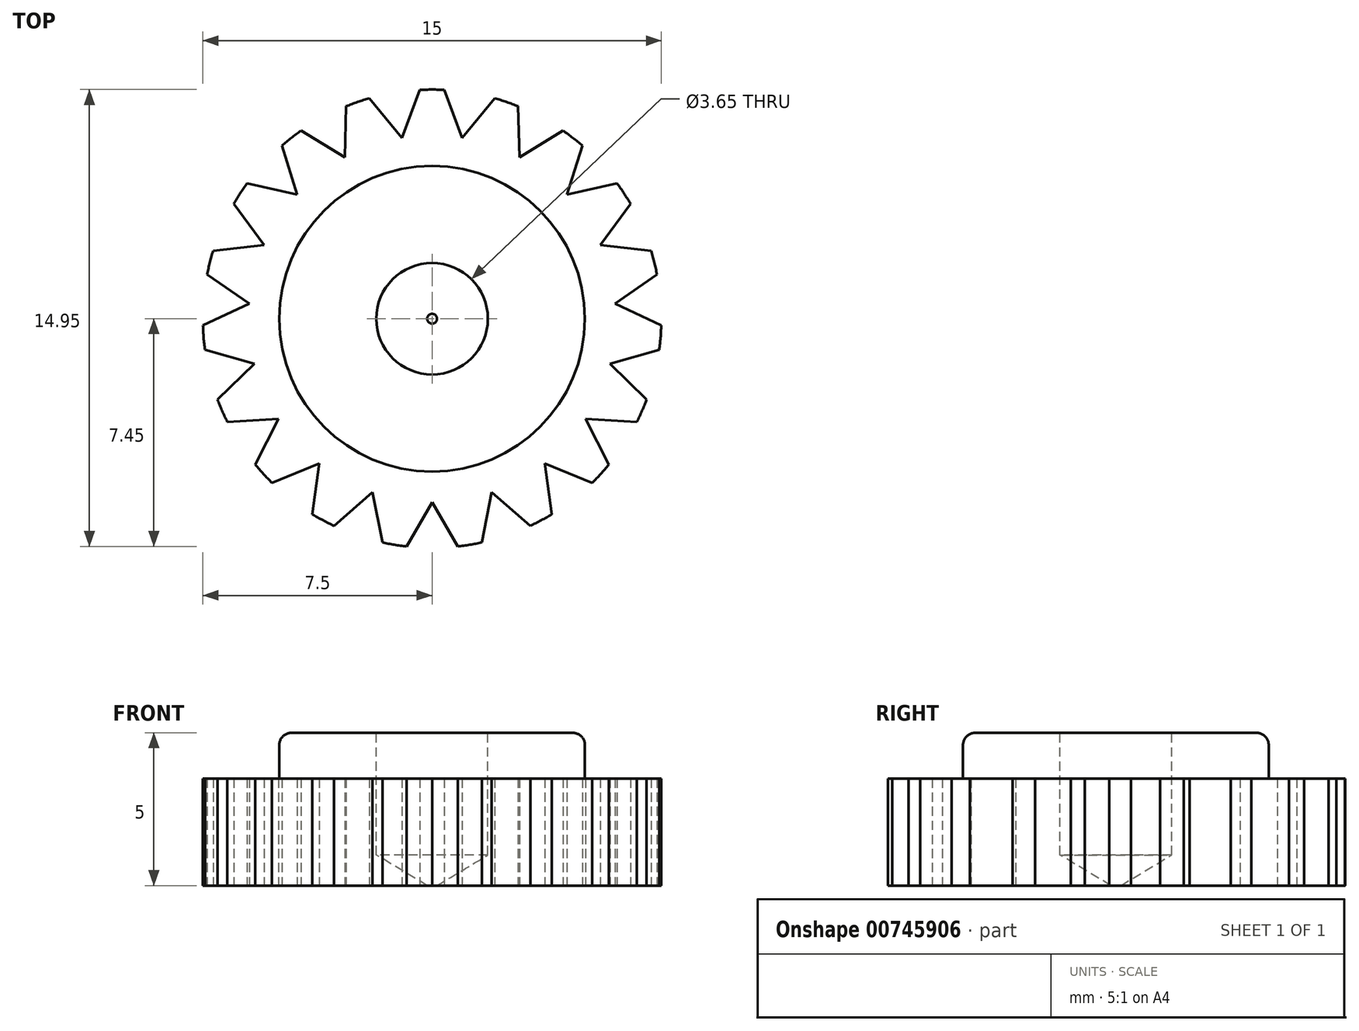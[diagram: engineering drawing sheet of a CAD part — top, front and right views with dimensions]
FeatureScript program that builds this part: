
annotation { "Feature Type Name" : "Feature", "Feature Type Description" : "" }
export const myFeature = defineFeature(function(context is Context, id is Id, definition is map)
    precondition{}
    {
        {
            var Q0;
            Q0=qCreatedBy(makeId("Top.planeOp"),FACE);
            var sketch = newSketch(context, id + "F0", { "sketchPlane" : qUnion([Q0])});
            skCircle(sketch, "E0", {"center": v(0, 0) * mm, "radius": 7.5 * mm});
            skCircle(sketch, "E1", {"center": v(0, 0) * mm, "radius": 5 * mm});
            skCircle(sketch, "E2.cCircle", {"center": v(0, -7.32) * mm, "radius": 1.31 * mm, "construction": true});
            skLineSegment(sketch, "E2.0", {"start": v(0, -6) * mm, "end": v(1.14, -7.97) * mm});
            skLineSegment(sketch, "E2.1", {"start": v(1.14, -7.97) * mm, "end": v(-1.14, -7.97) * mm});
            skLineSegment(sketch, "E2.2", {"start": v(-1.14, -7.97) * mm, "end": v(0, -6) * mm});
            skLineSegment(sketch, "E3.1.0", {"start": v(-1.95, -5.68) * mm, "end": v(-1.51, -7.91) * mm});
            skLineSegment(sketch, "E3.1.1", {"start": v(-3.67, -7.17) * mm, "end": v(-1.95, -5.68) * mm});
            skLineSegment(sketch, "E3.1.2", {"start": v(-1.51, -7.91) * mm, "end": v(-3.67, -7.17) * mm});
            skLineSegment(sketch, "E3.2.0", {"start": v(-3.69, -4.74) * mm, "end": v(-4, -7) * mm});
            skLineSegment(sketch, "E3.2.1", {"start": v(-5.8, -5.6) * mm, "end": v(-3.69, -4.74) * mm});
            skLineSegment(sketch, "E3.2.2", {"start": v(-4, -7) * mm, "end": v(-5.8, -5.6) * mm});
            skLineSegment(sketch, "E3.3.0", {"start": v(-5.03, -3.28) * mm, "end": v(-6.05, -5.31) * mm});
            skLineSegment(sketch, "E3.3.1", {"start": v(-7.3, -3.4) * mm, "end": v(-5.03, -3.28) * mm});
            skLineSegment(sketch, "E3.3.2", {"start": v(-6.05, -5.31) * mm, "end": v(-7.3, -3.4) * mm});
            skLineSegment(sketch, "E3.4.0", {"start": v(-5.82, -1.47) * mm, "end": v(-7.45, -3.06) * mm});
            skLineSegment(sketch, "E3.4.1", {"start": v(-8, -0.85) * mm, "end": v(-5.82, -1.47) * mm});
            skLineSegment(sketch, "E3.4.2", {"start": v(-7.45, -3.06) * mm, "end": v(-8, -0.85) * mm});
            skLineSegment(sketch, "E3.5.0", {"start": v(-5.98, 0.5) * mm, "end": v(-8.04, -0.48) * mm});
            skLineSegment(sketch, "E3.5.1", {"start": v(-7.85, 1.8) * mm, "end": v(-5.98, 0.5) * mm});
            skLineSegment(sketch, "E3.5.2", {"start": v(-8.04, -0.48) * mm, "end": v(-7.85, 1.8) * mm});
            skLineSegment(sketch, "E3.6.0", {"start": v(-5.5, 2.41) * mm, "end": v(-7.76, 2.16) * mm});
            skLineSegment(sketch, "E3.6.1", {"start": v(-6.85, 4.25) * mm, "end": v(-5.5, 2.41) * mm});
            skLineSegment(sketch, "E3.6.2", {"start": v(-7.76, 2.16) * mm, "end": v(-6.85, 4.25) * mm});
            skLineSegment(sketch, "E3.7.0", {"start": v(-4.42, 4.07) * mm, "end": v(-6.64, 4.56) * mm});
            skLineSegment(sketch, "E3.7.1", {"start": v(-5.1, 6.24) * mm, "end": v(-4.42, 4.07) * mm});
            skLineSegment(sketch, "E3.7.2", {"start": v(-6.64, 4.56) * mm, "end": v(-5.1, 6.24) * mm});
            skLineSegment(sketch, "E3.8.0", {"start": v(-2.86, 5.28) * mm, "end": v(-4.8, 6.47) * mm});
            skLineSegment(sketch, "E3.8.1", {"start": v(-2.8, 7.55) * mm, "end": v(-2.86, 5.28) * mm});
            skLineSegment(sketch, "E3.8.2", {"start": v(-4.8, 6.47) * mm, "end": v(-2.8, 7.55) * mm});
            skLineSegment(sketch, "E3.9.0", {"start": v(-0.99, 5.92) * mm, "end": v(-2.44, 7.68) * mm});
            skLineSegment(sketch, "E3.9.1", {"start": v(-0.19, 8.05) * mm, "end": v(-0.99, 5.92) * mm});
            skLineSegment(sketch, "E3.9.2", {"start": v(-2.44, 7.68) * mm, "end": v(-0.19, 8.05) * mm});
            skLineSegment(sketch, "E3.10.0", {"start": v(0.99, 5.92) * mm, "end": v(0.19, 8.05) * mm});
            skLineSegment(sketch, "E3.10.1", {"start": v(2.44, 7.68) * mm, "end": v(0.99, 5.92) * mm});
            skLineSegment(sketch, "E3.10.2", {"start": v(0.19, 8.05) * mm, "end": v(2.44, 7.68) * mm});
            skLineSegment(sketch, "E3.11.0", {"start": v(2.86, 5.28) * mm, "end": v(2.8, 7.55) * mm});
            skLineSegment(sketch, "E3.11.1", {"start": v(4.8, 6.47) * mm, "end": v(2.86, 5.28) * mm});
            skLineSegment(sketch, "E3.11.2", {"start": v(2.8, 7.55) * mm, "end": v(4.8, 6.47) * mm});
            skLineSegment(sketch, "E3.12.0", {"start": v(4.42, 4.07) * mm, "end": v(5.1, 6.24) * mm});
            skLineSegment(sketch, "E3.12.1", {"start": v(6.64, 4.56) * mm, "end": v(4.42, 4.07) * mm});
            skLineSegment(sketch, "E3.12.2", {"start": v(5.1, 6.24) * mm, "end": v(6.64, 4.56) * mm});
            skLineSegment(sketch, "E3.13.0", {"start": v(5.5, 2.41) * mm, "end": v(6.85, 4.25) * mm});
            skLineSegment(sketch, "E3.13.1", {"start": v(7.76, 2.16) * mm, "end": v(5.5, 2.41) * mm});
            skLineSegment(sketch, "E3.13.2", {"start": v(6.85, 4.25) * mm, "end": v(7.76, 2.16) * mm});
            skLineSegment(sketch, "E3.14.0", {"start": v(5.98, 0.5) * mm, "end": v(7.85, 1.8) * mm});
            skLineSegment(sketch, "E3.14.1", {"start": v(8.04, -0.48) * mm, "end": v(5.98, 0.5) * mm});
            skLineSegment(sketch, "E3.14.2", {"start": v(7.85, 1.8) * mm, "end": v(8.04, -0.48) * mm});
            skLineSegment(sketch, "E3.15.0", {"start": v(5.82, -1.47) * mm, "end": v(8, -0.85) * mm});
            skLineSegment(sketch, "E3.15.1", {"start": v(7.45, -3.06) * mm, "end": v(5.82, -1.47) * mm});
            skLineSegment(sketch, "E3.15.2", {"start": v(8, -0.85) * mm, "end": v(7.45, -3.06) * mm});
            skLineSegment(sketch, "E3.16.0", {"start": v(5.03, -3.28) * mm, "end": v(7.3, -3.4) * mm});
            skLineSegment(sketch, "E3.16.1", {"start": v(6.05, -5.31) * mm, "end": v(5.03, -3.28) * mm});
            skLineSegment(sketch, "E3.16.2", {"start": v(7.3, -3.4) * mm, "end": v(6.05, -5.31) * mm});
            skLineSegment(sketch, "E3.17.0", {"start": v(3.69, -4.74) * mm, "end": v(5.8, -5.6) * mm});
            skLineSegment(sketch, "E3.17.1", {"start": v(4, -7) * mm, "end": v(3.69, -4.74) * mm});
            skLineSegment(sketch, "E3.17.2", {"start": v(5.8, -5.6) * mm, "end": v(4, -7) * mm});
            skLineSegment(sketch, "E3.18.0", {"start": v(1.95, -5.68) * mm, "end": v(3.67, -7.17) * mm});
            skLineSegment(sketch, "E3.18.1", {"start": v(1.51, -7.91) * mm, "end": v(1.95, -5.68) * mm});
            skLineSegment(sketch, "E3.18.2", {"start": v(3.67, -7.17) * mm, "end": v(1.51, -7.91) * mm});
            skLineSegment(sketch, "E3.anchor1", {"start": v(0, 0) * mm, "end": v(1.14, -7.97) * mm, "construction": true});
            skLineSegment(sketch, "E3.anchor2", {"start": v(0, 0) * mm, "end": v(1.14, -7.97) * mm, "construction": true});
            skSolve(sketch);
        }
        {
            var Q0;
            Q0=makeQuery(id+"F0.imprint","IMPRINT",FACE,{"disambiguationData":[TD([[makeQuery(id+"F0.imprint","IMPRINT",EDGE,{"derivedFrom":sQuery(id+"F0.wireOp",EDGE,"E0")}),1.0]])]});
            extrude(context, id + "F1", {"entities" : qUnion([Q0]), "depth" : 3.5 * mm, "offsetDistance" : 25 * mm});
        }
        {
            var Q0;
            Q0=makeQuery(id+"F0.imprint","IMPRINT",FACE,{"disambiguationData":[TD([[makeQuery(id+"F0.imprint","IMPRINT",EDGE,{"derivedFrom":sQuery(id+"F0.wireOp",EDGE,"E1")}),1.0]])]});
            extrude(context, id + "F2", {"entities" : qUnion([Q0]), "operationType" : NewBodyOperationType.ADD, "depth" : 5 * mm, "offsetDistance" : 25 * mm});
        }
        {
            var Q0;
            Q0=makeQuery(id+"F2.opExtrude","CAP_FACE",FACE,{"disambiguationData":[OSD([sQuery(id+"F0.wireOp",EDGE,"E1")])],"isStart":false});
            var sketch = newSketch(context, id + "F3", { "sketchPlane" : qUnion([Q0])});
            skPoint(sketch, "E4", {"position": v(0, 0) * mm});
            skSolve(sketch);
        }
        {
            var Q0;
            Q0=sQuery(id+"F3.wireOp",VERTEX,"E4");
            var Q1;
            Q1=makeQuery(id+"F1.opExtrude","SWEPT_BODY",BODY,{"disambiguationData":[OSD([sQuery(id+"F0.wireOp",EDGE,"E0"),sQuery(id+"F0.wireOp",EDGE,"E1")])]});
            hole(context, id + "F4", {"style" : HoleStyle.SIMPLE, "endStyle" : HoleEndStyle.BLIND, "holeDiameter" : 3.65 * mm, "majorDiameter" : 5 * mm, "holeDepth" : 4 * mm, "isTappedThrough" : true, "tappedDepth" : 12 * mm, "tapClearance" : 3, "startFromSketch" : true, "locations" : qUnion([Q0]), "scope" : qUnion([Q1])});
        }
        {
            var Q0;
            Q0=makeQuery(id+"F2.opExtrude","CAP_EDGE",EDGE,{"disambiguationData":[OSD([sQuery(id+"F0.wireOp",EDGE,"E1")])],"isStart":false});
            fillet(context, id + "F5", {"entities" : qUnion([Q0]), "radius" : 0.4 * mm, "tangentPropagation" : true, "allowEdgeOverflow" : false});
        }
    });
